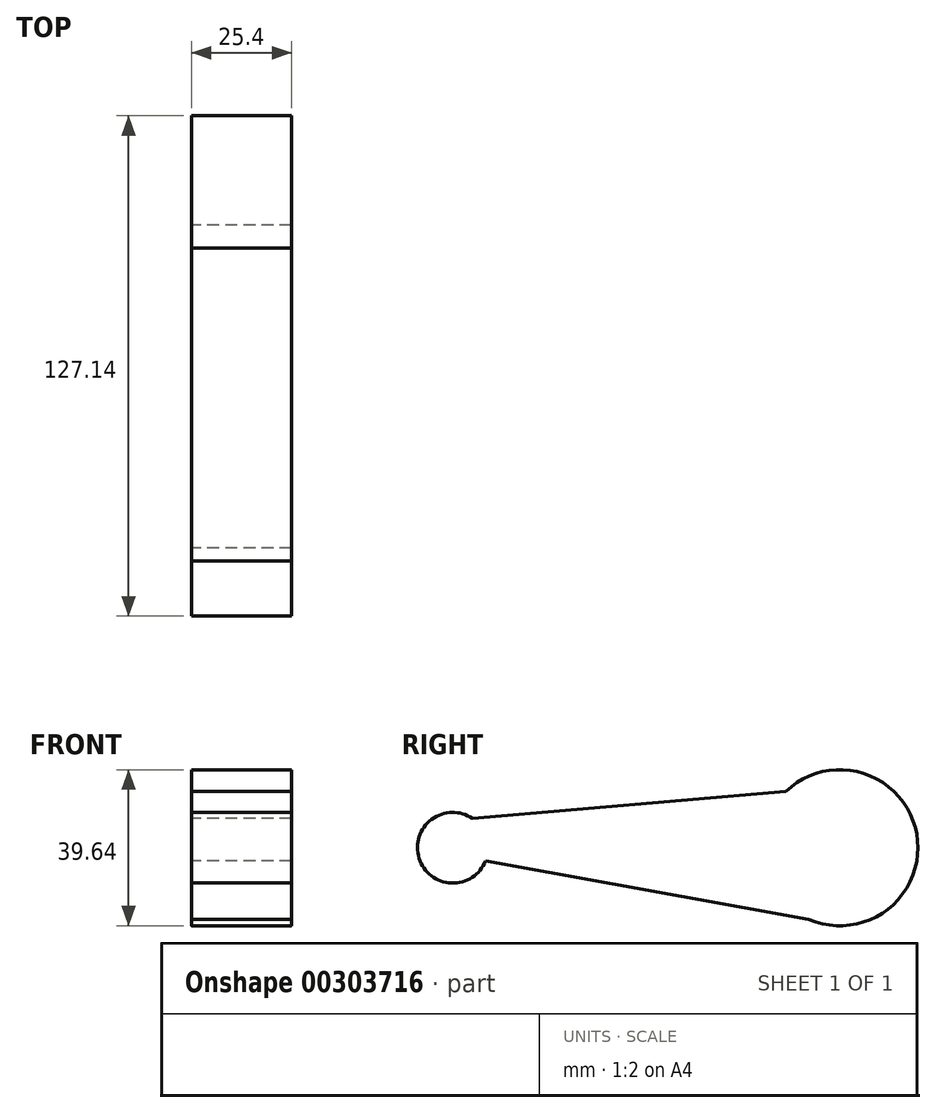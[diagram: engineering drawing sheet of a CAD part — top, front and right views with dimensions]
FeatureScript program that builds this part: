
annotation { "Feature Type Name" : "Feature", "Feature Type Description" : "" }
export const myFeature = defineFeature(function(context is Context, id is Id, definition is map)
    precondition{}
    {
        {
            var Q0;
            Q0=qCreatedBy(makeId("Right.planeOp"),FACE);
            var sketch = newSketch(context, id + "F0", { "sketchPlane" : qUnion([Q0])});
            skCircle(sketch, "E0", {"center": v(2.4, 0) * mm, "radius": 19.82 * mm});
            skCircle(sketch, "E1", {"center": v(-95.94, 0) * mm, "radius": 8.98 * mm});
            skLineSegment(sketch, "E2", {"start": v(-87.6, -3.3) * mm, "end": v(-5.56, -18.16) * mm});
            skLineSegment(sketch, "E3", {"start": v(-11.35, 14.28) * mm, "end": v(-90.93, 7.44) * mm});
            skSolve(sketch);
        }
        {
            var Q0;
            Q0=qCreatedBy(makeId("Right.planeOp"),FACE);
            var sketch = newSketch(context, id + "F1", { "sketchPlane" : qUnion([Q0])});
            skLineSegment(sketch, "E4", {"start": v(-90.46, 8.4) * mm, "end": v(-88.06, -4.63) * mm});
            skSolve(sketch);
        }
        {
            var Q0;
            Q0 = qSketchRegion(id + "F1", true);
            var Q1;
            {var subQ0=sQuery(id+"F0.wireOp",EDGE,"E2");Q1=makeQuery(id+"F0.imprint","IMPRINT",FACE,{"disambiguationData":[TD([[makeQuery(id+"F0.imprint","IMPRINT",EDGE,{"derivedFrom":subQ0}),1.0]])]});}
            var Q2;
            {var subQ0=sQuery(id+"F0.wireOp",EDGE,"E1");var subQ1=makeQuery(id+"F0.imprint","INTERSECT",VERTEX,{"derivedFrom":[subQ0,sQuery(id+"F0.wireOp",EDGE,"E2")]});Q2=makeQuery(id+"F0.imprint","IMPRINT",FACE,{"disambiguationData":[TD([[makeQuery(id+"F0.imprint","IMPRINT",EDGE,{"disambiguationData":[TD([[subQ1,1.0]])],"derivedFrom":subQ0}),1.0]])]});}
            var Q3;
            {var subQ0=sQuery(id+"F0.wireOp",EDGE,"E0");var subQ1=makeQuery(id+"F0.imprint","INTERSECT",VERTEX,{"derivedFrom":[subQ0,sQuery(id+"F0.wireOp",EDGE,"E2")]});Q3=makeQuery(id+"F0.imprint","IMPRINT",FACE,{"disambiguationData":[TD([[makeQuery(id+"F0.imprint","IMPRINT",EDGE,{"disambiguationData":[TD([[subQ1,1.0]])],"derivedFrom":subQ0}),1.0]])]});}
            extrude(context, id + "F2", {"entities" : qUnion([Q0, Q1, Q2, Q3]), "depth" : 25.4 * mm});
        }
        {
            var Q0;
            Q0 = qSketchRegion(id + "F0", true);
            extrude(context, id + "F3", {"entities" : qUnion([Q0]), "operationType" : NewBodyOperationType.ADD, "depth" : 25.4 * mm});
        }
    });
